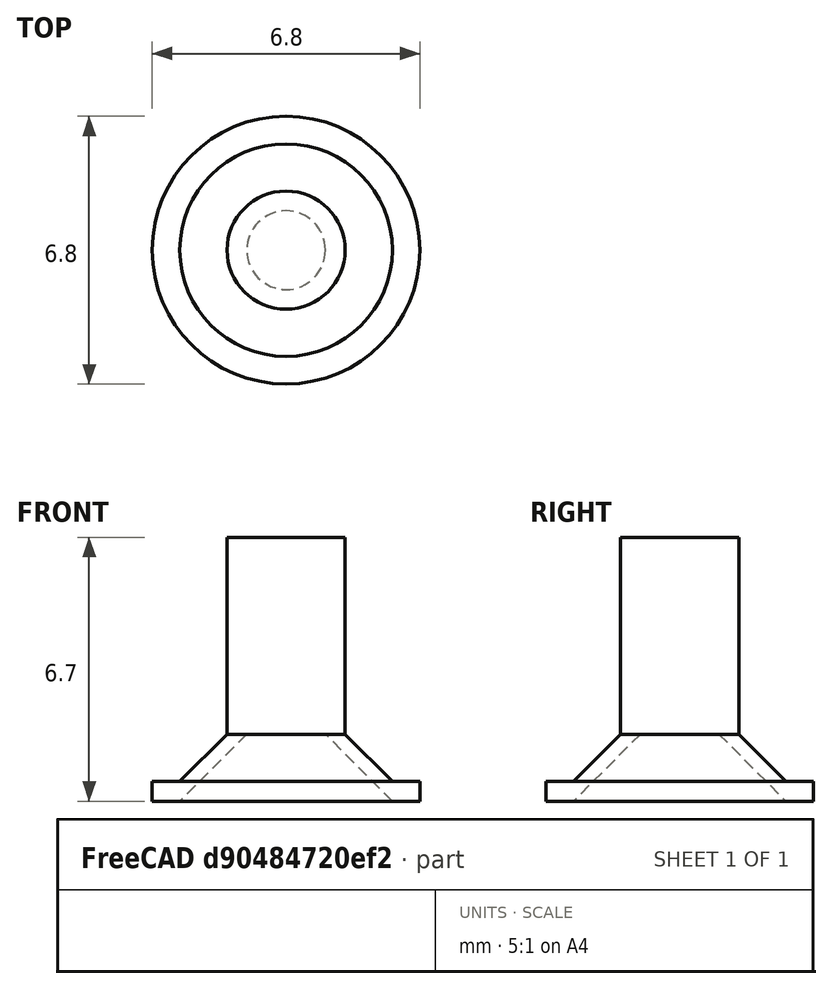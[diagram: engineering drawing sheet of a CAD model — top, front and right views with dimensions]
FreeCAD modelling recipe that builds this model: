
FCSTD DOCUMENT  (FreeCAD 0.19R24267 +99 (Git))
Label: buttonv2
License: All rights reserved
LicenseURL: http://en.wikipedia.org/wiki/All_rights_reserved
objects: Sketcher::SketchObject×1, PartDesign::Revolution×1, PartDesign::Body×1
note: 4 computed .brp shape members not serialized (recipe doc carries the construction recipe); baked Part::Feature solids carry a one-line shape summary decoded from their .brp

FEATURE [Sketcher::SketchObject] Sketch
  FullyConstrained = true
  MapMode = 5
  Placement = pos=(0,0,0) rot=(1,0,0;1.5708rad)
  Support = -> [XZ_Plane]
  sketch-geometry (10):
    g0: LineSegment StartX=0 StartY=6.7 StartZ=0 EndX=1.5 EndY=6.7 EndZ=0
    g1: LineSegment StartX=1.5 StartY=6.7 StartZ=0 EndX=1.5 EndY=1.7 EndZ=0
    g2: LineSegment StartX=1.5 StartY=1.7 StartZ=0 EndX=2.7 EndY=0.5 EndZ=0
    g3: LineSegment StartX=2.7 StartY=0.5 StartZ=0 EndX=3.4 EndY=0.5 EndZ=0
    g4: LineSegment StartX=3.4 StartY=0.5 StartZ=0 EndX=3.4 EndY=0 EndZ=0
    g5: LineSegment StartX=3.4 StartY=0 StartZ=0 EndX=2.7 EndY=0 EndZ=0
    g6: LineSegment StartX=2.7 StartY=0 StartZ=0 EndX=1 EndY=1.7 EndZ=0
    g7: LineSegment StartX=1 StartY=1.7 StartZ=0 EndX=0 EndY=1.7 EndZ=0
    g8: LineSegment StartX=0 StartY=1.7 StartZ=0 EndX=0 EndY=6.7 EndZ=0
    g9: LineSegment StartX=1 StartY=1.7 StartZ=0 EndX=1.5 EndY=1.7 EndZ=0
  constraints (29):
    c: PointOnObject(g0,g-2)
    c: Horizontal(g0)
    c: Coincident(g1,g0)
    c: Vertical(g1)
    c: Coincident(g2,g1)
    c: Coincident(g3,g2)
    c: Horizontal(g3)
    c: Coincident(g4,g3)
    c: PointOnObject(g4,g-1)
    c: Vertical(g4)
    c: Coincident(g5,g4)
    c: Horizontal(g5)
    c: Coincident(g6,g5)
    c: Coincident(g7,g6)
    c: Horizontal(g7)
    c: Coincident(g8,g7)
    c: Coincident(g8,g0)
    c: Vertical(g8)
    c: Parallel(g6,g2)
    c: DistanceX(g0,g0) = 1.5
    c: DistanceY(g1,g1) = 5
    c: DistanceX(g-1,g4) = 3.4
    c: Coincident(g9,g6)
    c: Coincident(g9,g1)
    c: Horizontal(g9)
    c: Angle(g5,g6) = 2.35619
    c: DistanceX(g7,g7) = 1
    c: DistanceY(g4,g4) = 0.5
    c: DistanceX(g3,g3) = 0.7
FEATURE [PartDesign::Revolution] Revolution
  Angle = 360
  Axis = (0,-2e-16,1)
  Base = (0,0,0)
  Placement = pos=(0,0,0) rot=(1,0,0;1.5708rad)
  Profile = -> Sketch
  ReferenceAxis = -> Sketch [V_Axis]
  Reversed = true
FEATURE [PartDesign::Body] Body
  Group = -> [Sketch,Revolution]
  Origin = -> Origin
  Tip = -> Revolution
